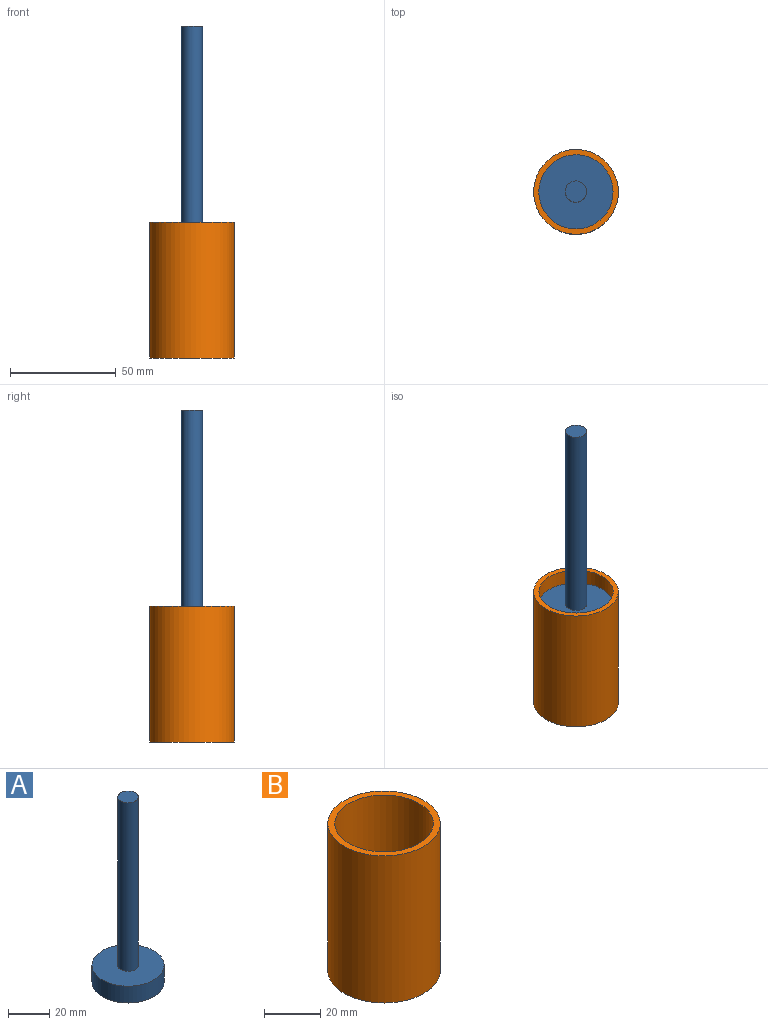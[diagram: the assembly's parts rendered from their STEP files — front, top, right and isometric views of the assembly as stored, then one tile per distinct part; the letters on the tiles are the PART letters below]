
ASSEMBLY  parts=2 mates=1
PART A: 5 faces, bbox 35x35x110 mm
  f0: cylinder r=17.5mm len=35mm, axis (0,0,1), area 1099.6mm2, adj f1,f2
  f1: plane 35x35mm, normal (0,0,-1), area 962.1mm2, adj f0
  f2: plane 35x35mm, normal (0,0,1), area 883.6mm2, adj f0,f3
  f3: cylinder r=5mm len=100mm, axis (0,0,-1), area 3141.6mm2, adj f2,f4
  f4: plane 10x10mm, normal (0,0,1), area 78.5mm2, adj f3
PART B: 5 faces, bbox 40x40x64 mm
  f0: cylinder r=20mm len=64mm, axis (0,0,1), area 8042.5mm2, adj f1,f2
  f1: plane 40x40mm, normal (0,0,-1), area 1256.6mm2, adj f0
  f2: plane 40x40mm, normal (0,0,1), area 294.5mm2, adj f0,f3
  f3: cylinder r=17.5mm len=40mm, axis (0,0,1), area 4398.2mm2, adj f2,f4
  f4: plane 35x35mm, normal (0,0,1), area 962.1mm2, adj f3
PLACE A t=(31.4,16.01,-54.77)mm
PLACE B t=(31.4,16.01,-47.42)mm
MATE cylindrical B.f0 <-> A.f0  axis (0,0,1) through (31.4,16.01,-47.42)mm
